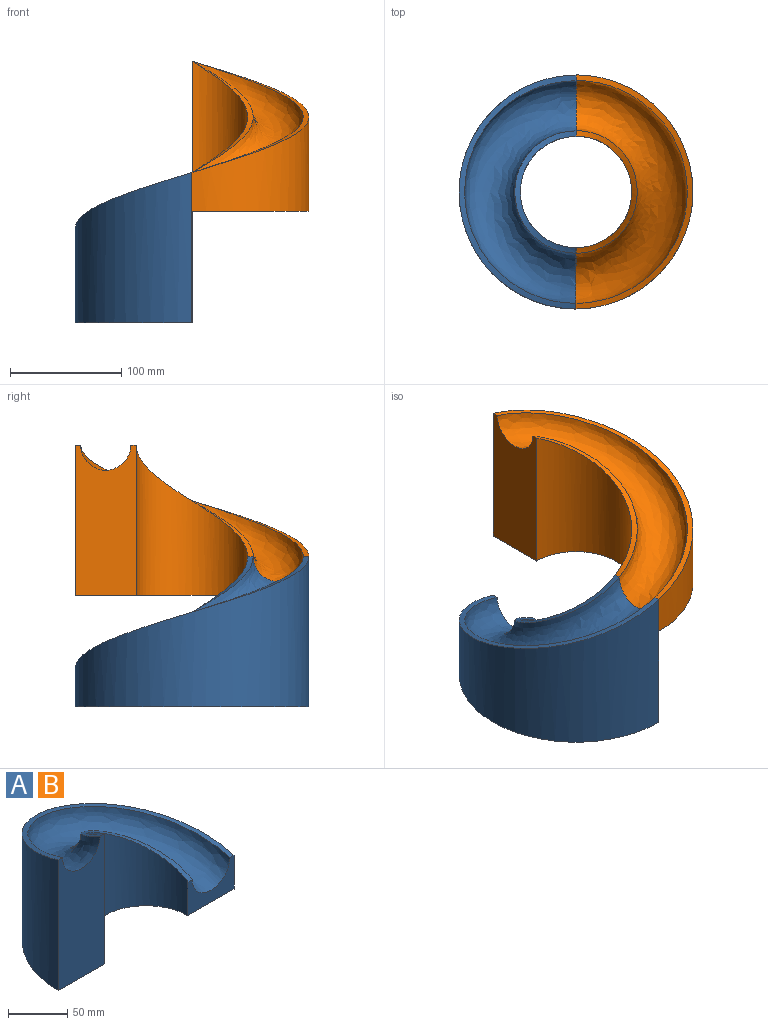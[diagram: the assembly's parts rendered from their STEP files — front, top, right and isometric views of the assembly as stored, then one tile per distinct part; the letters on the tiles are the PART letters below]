
ASSEMBLY  parts=2 mates=1
PART A: 8 faces, bbox 210x105x145 mm
  f0: plane 135x55mm, normal (0,-1,0), area 6629.8mm2, adj f2,f3,f4,f5,f6,f7
  f1: plane 55x35mm, normal (0,-1,0), area 1129.8mm2, adj f2,f3,f4,f5,f6,f7
  f2: cylinder r=105mm len=210mm, axis (0,0,-1), area 28039mm2, adj f0,f1,f3,f7
  f3: bspline ~210x105mm, area 1686mm2, adj f0,f1,f2,f4
  f4: bspline ~200x145mm, area 17929.6mm2, adj f0,f1,f3,f5
  f5: bspline ~110x100mm, area 964.6mm2, adj f0,f1,f4,f6
  f6: cylinder r=50mm len=135mm, axis (0,0,-1), area 13351.9mm2, adj f0,f1,f5,f7
  f7: plane 210x105mm, normal (0,0,-1), area 13391mm2, adj f0,f1,f2,f6
PART B: same geometry as A
PLACE A rot(axis=(0,0,1),90deg) t=(-156.87,-181.16,-293.29)mm
PLACE B rot(axis=(0,0,-1),90deg) t=(-156.87,-281.16,-193.29)mm
MATE fastened A.f0 <-> B.f1  axis (1,0,0) through (-156.87,-308.66,-158.29)mm
